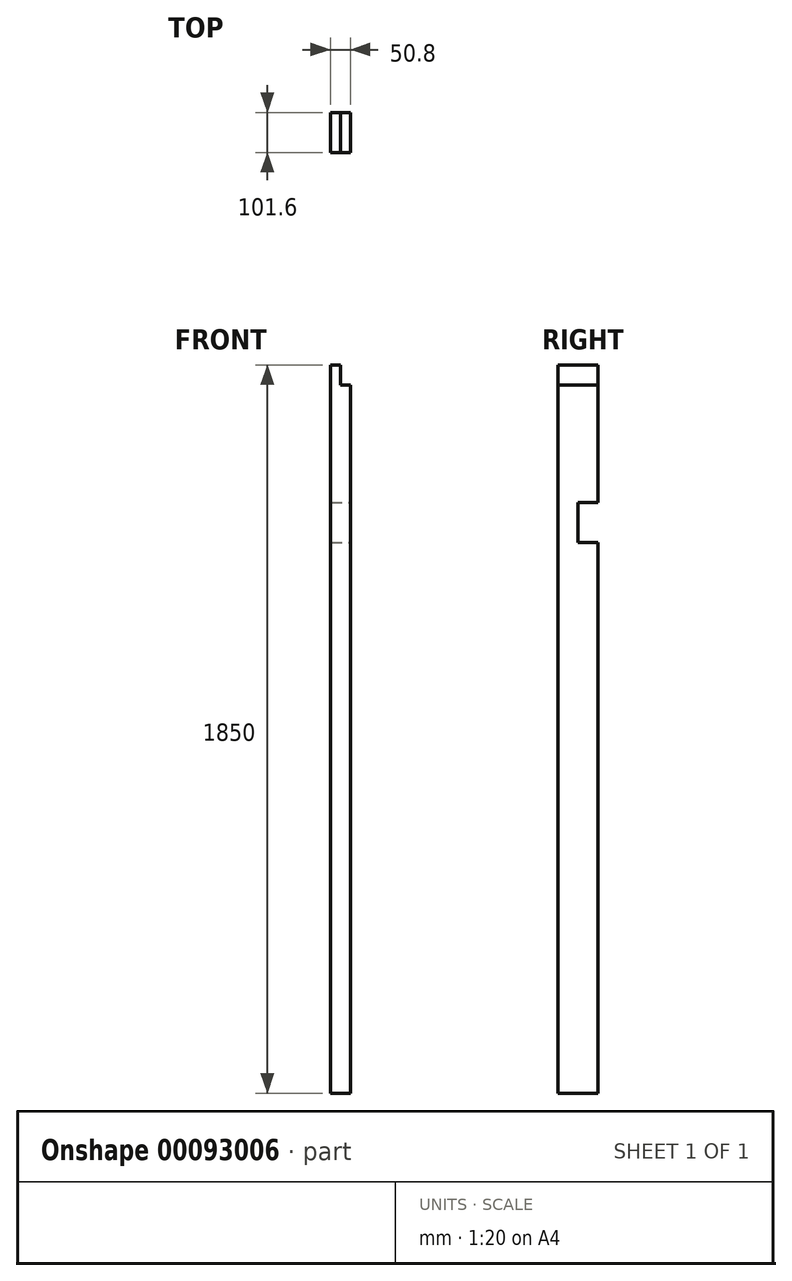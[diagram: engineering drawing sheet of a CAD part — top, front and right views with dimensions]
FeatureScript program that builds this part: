
annotation { "Feature Type Name" : "Feature", "Feature Type Description" : "" }
export const myFeature = defineFeature(function(context is Context, id is Id, definition is map)
    precondition{}
    {
        {
            var Q0;
            Q0=qCreatedBy(makeId("Top.planeOp"),FACE);
            var sketch = newSketch(context, id + "F0", { "sketchPlane" : qUnion([Q0])});
            skLineSegment(sketch, "E0.bottom", {"start": v(25.4, 50.8) * mm, "end": v(-25.4, 50.8) * mm});
            skLineSegment(sketch, "E0.top", {"start": v(25.4, -50.8) * mm, "end": v(-25.4, -50.8) * mm});
            skLineSegment(sketch, "E0.left", {"start": v(25.4, 50.8) * mm, "end": v(25.4, -50.8) * mm});
            skLineSegment(sketch, "E0.right", {"start": v(-25.4, 50.8) * mm, "end": v(-25.4, -50.8) * mm});
            skPoint(sketch, "E0.middle", {"position": v(0, 0) * mm});
            skSolve(sketch);
        }
        {
            var Q0;
            Q0=makeQuery(id+"F0.imprint","IMPRINT",FACE,{"disambiguationData":[TD([[makeQuery(id+"F0.imprint","IMPRINT",EDGE,{"derivedFrom":sQuery(id+"F0.wireOp",EDGE,"E0.bottom")}),1.0]])]});
            extrude(context, id + "F1", {"entities" : qUnion([Q0]), "depth" : 1850 * mm});
        }
        {
            var Q0;
            Q0=qCreatedBy(makeId("Right.planeOp"),FACE);
            var sketch = newSketch(context, id + "F2", { "sketchPlane" : qUnion([Q0])});
            skLineSegment(sketch, "E1.bottom", {"start": v(0, 1500) * mm, "end": v(50.8, 1500) * mm});
            skLineSegment(sketch, "E1.top", {"start": v(0, 1398.4) * mm, "end": v(50.8, 1398.4) * mm});
            skLineSegment(sketch, "E1.left", {"start": v(0, 1500) * mm, "end": v(0, 1398.4) * mm});
            skLineSegment(sketch, "E1.right", {"start": v(50.8, 1500) * mm, "end": v(50.8, 1398.4) * mm});
            skSolve(sketch);
        }
        {
            var Q0;
            Q0 = qSketchRegion(id + "F2", true);
            extrude(context, id + "F3", {"entities" : qUnion([Q0]), "operationType" : NewBodyOperationType.REMOVE, "endBound" : BoundingType.SYMMETRIC, "oppositeDirection" : true, "depth" : 100 * mm});
        }
        {
            var Q0;
            Q0=makeQuery(id+"F1.opExtrude","CAP_FACE",FACE,{"disambiguationData":[OSD([sQuery(id+"F0.wireOp",EDGE,"E0.bottom"),sQuery(id+"F0.wireOp",EDGE,"E0.top"),sQuery(id+"F0.wireOp",EDGE,"E0.left"),sQuery(id+"F0.wireOp",EDGE,"E0.right")])],"isStart":false});
            var sketch = newSketch(context, id + "F4", { "sketchPlane" : qUnion([Q0])});
            skLineSegment(sketch, "E2.bottom", {"start": v(25.4, 50.8) * mm, "end": v(0, 50.8) * mm});
            skLineSegment(sketch, "E2.top", {"start": v(25.4, -50.8) * mm, "end": v(0, -50.8) * mm});
            skLineSegment(sketch, "E2.left", {"start": v(25.4, 50.8) * mm, "end": v(25.4, -50.8) * mm});
            skLineSegment(sketch, "E2.right", {"start": v(0, 50.8) * mm, "end": v(0, -50.8) * mm});
            skSolve(sketch);
        }
        {
            var Q0;
            Q0=makeQuery(id+"F4.imprint","IMPRINT",FACE,{"disambiguationData":[TD([[makeQuery(id+"F4.imprint","IMPRINT",EDGE,{"derivedFrom":sQuery(id+"F4.wireOp",EDGE,"E2.bottom")}),1.0]])]});
            extrude(context, id + "F5", {"entities" : qUnion([Q0]), "operationType" : NewBodyOperationType.REMOVE, "oppositeDirection" : true, "depth" : 50.8 * mm});
        }
    });
